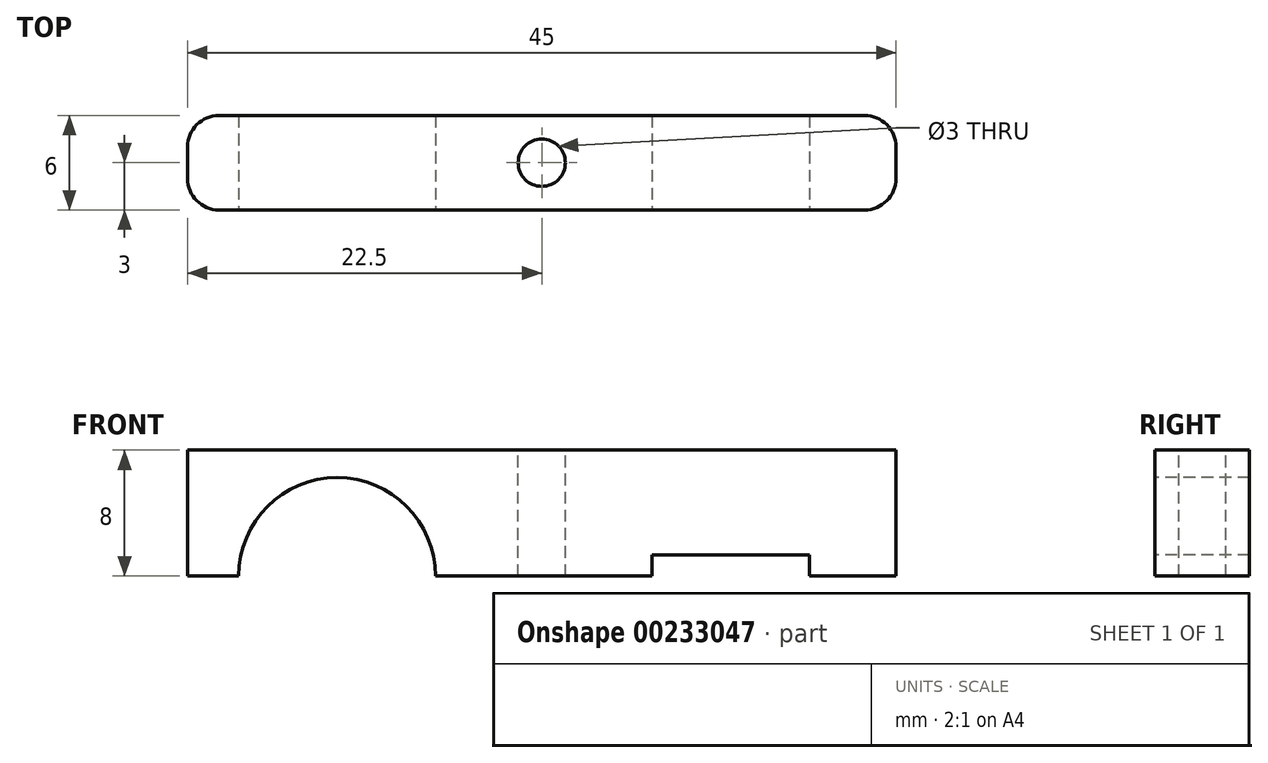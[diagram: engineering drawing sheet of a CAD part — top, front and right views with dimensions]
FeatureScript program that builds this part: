
annotation { "Feature Type Name" : "Feature", "Feature Type Description" : "" }
export const myFeature = defineFeature(function(context is Context, id is Id, definition is map)
    precondition{}
    {
        {
            var Q0;
            Q0=qCreatedBy(makeId("Top.planeOp"),FACE);
            var sketch = newSketch(context, id + "F0", { "sketchPlane" : qUnion([Q0])});
            skLineSegment(sketch, "E0.bottom", {"start": v(-22.5, 3) * mm, "end": v(22.5, 3) * mm});
            skLineSegment(sketch, "E0.top", {"start": v(-22.5, -3) * mm, "end": v(22.5, -3) * mm});
            skLineSegment(sketch, "E0.left", {"start": v(-22.5, 3) * mm, "end": v(-22.5, -3) * mm});
            skLineSegment(sketch, "E0.right", {"start": v(22.5, 3) * mm, "end": v(22.5, -3) * mm});
            skSolve(sketch);
        }
        {
            var Q0;
            Q0 = qSketchRegion(id + "F0", true);
            extrude(context, id + "F1", {"entities" : qUnion([Q0]), "depth" : 8 * mm});
        }
        {
            var Q0;
            Q0=makeQuery(id+"F1.opExtrude","SWEPT_FACE",FACE,{"disambiguationData":[OSD([sQuery(id+"F0.wireOp",EDGE,"E0.top")])]});
            var sketch = newSketch(context, id + "F2", { "sketchPlane" : qUnion([Q0])});
            skCircle(sketch, "E1", {"center": v(-13, 0) * mm, "radius": 6.25 * mm});
            skLineSegment(sketch, "E2.bottom", {"start": v(7, 1.35) * mm, "end": v(17, 1.35) * mm});
            skLineSegment(sketch, "E2.top", {"start": v(7, -1.35) * mm, "end": v(17, -1.35) * mm});
            skLineSegment(sketch, "E2.left", {"start": v(7, 1.35) * mm, "end": v(7, -1.35) * mm});
            skLineSegment(sketch, "E2.right", {"start": v(17, 1.35) * mm, "end": v(17, -1.35) * mm});
            skSolve(sketch);
        }
        {
            var Q0;
            {var subQ0=sQuery(id+"F2.wireOp",EDGE,"E1");var subQ1=makeQuery(id+"F1.opExtrude","CAP_EDGE",EDGE,{"disambiguationData":[OSD([sQuery(id+"F0.wireOp",EDGE,"E0.top")])],"isStart":true});var subQ2=makeQuery(id+"F2.imprint","INTERSECT",VERTEX,{"disambiguationData":[OD(0.0)],"derivedFrom":[subQ1,subQ0]});Q0=makeQuery(id+"F2.imprint","IMPRINT",FACE,{"disambiguationData":[TD([[makeQuery(id+"F2.imprint","IMPRINT",EDGE,{"disambiguationData":[TD([[subQ2,1.0]])],"derivedFrom":subQ0}),1.0]])]});}
            var Q1;
            {var subQ0=sQuery(id+"F2.wireOp",EDGE,"E2.bottom");Q1=makeQuery(id+"F2.imprint","IMPRINT",FACE,{"disambiguationData":[TD([[makeQuery(id+"F2.imprint","IMPRINT",EDGE,{"derivedFrom":subQ0}),-1.0]])]});}
            extrude(context, id + "F3", {"entities" : qUnion([Q0, Q1]), "operationType" : NewBodyOperationType.REMOVE, "endBound" : BoundingType.THROUGH_ALL, "oppositeDirection" : true, "depth" : 25 * mm});
        }
        {
            var Q0;
            Q0=makeQuery(id+"F1.opExtrude","CAP_FACE",FACE,{"disambiguationData":[OSD([sQuery(id+"F0.wireOp",EDGE,"E0.bottom"),sQuery(id+"F0.wireOp",EDGE,"E0.top"),sQuery(id+"F0.wireOp",EDGE,"E0.left"),sQuery(id+"F0.wireOp",EDGE,"E0.right")])],"isStart":false});
            var sketch = newSketch(context, id + "F4", { "sketchPlane" : qUnion([Q0])});
            skCircle(sketch, "E3", {"center": v(0, 0) * mm, "radius": 1.5 * mm});
            skSolve(sketch);
        }
        {
            var Q0;
            Q0=makeQuery(id+"F4.imprint","IMPRINT",FACE,{"disambiguationData":[TD([[makeQuery(id+"F4.imprint","IMPRINT",EDGE,{"derivedFrom":sQuery(id+"F4.wireOp",EDGE,"E3")}),1.0]])]});
            extrude(context, id + "F5", {"entities" : qUnion([Q0]), "operationType" : NewBodyOperationType.REMOVE, "endBound" : BoundingType.THROUGH_ALL, "oppositeDirection" : true, "depth" : 25 * mm});
        }
        {
            var Q0;
            Q0=makeQuery(id+"F1.opExtrude","SWEPT_EDGE",EDGE,{"disambiguationData":[OSD([sQuery(id+"F0.wireOp",EDGE,"E0.top"),sQuery(id+"F0.wireOp",EDGE,"E0.left")])]});
            var Q1;
            Q1=makeQuery(id+"F1.opExtrude","SWEPT_EDGE",EDGE,{"disambiguationData":[OSD([sQuery(id+"F0.wireOp",EDGE,"E0.bottom"),sQuery(id+"F0.wireOp",EDGE,"E0.left")])]});
            var Q2;
            Q2=makeQuery(id+"F1.opExtrude","SWEPT_EDGE",EDGE,{"disambiguationData":[OSD([sQuery(id+"F0.wireOp",EDGE,"E0.top"),sQuery(id+"F0.wireOp",EDGE,"E0.right")])]});
            var Q3;
            Q3=makeQuery(id+"F1.opExtrude","SWEPT_EDGE",EDGE,{"disambiguationData":[OSD([sQuery(id+"F0.wireOp",EDGE,"E0.bottom"),sQuery(id+"F0.wireOp",EDGE,"E0.right")])]});
            fillet(context, id + "F6", {"entities" : qUnion([Q0, Q1, Q2, Q3]), "radius" : 2 * mm, "tangentPropagation" : true, "allowEdgeOverflow" : false});
        }
    });
